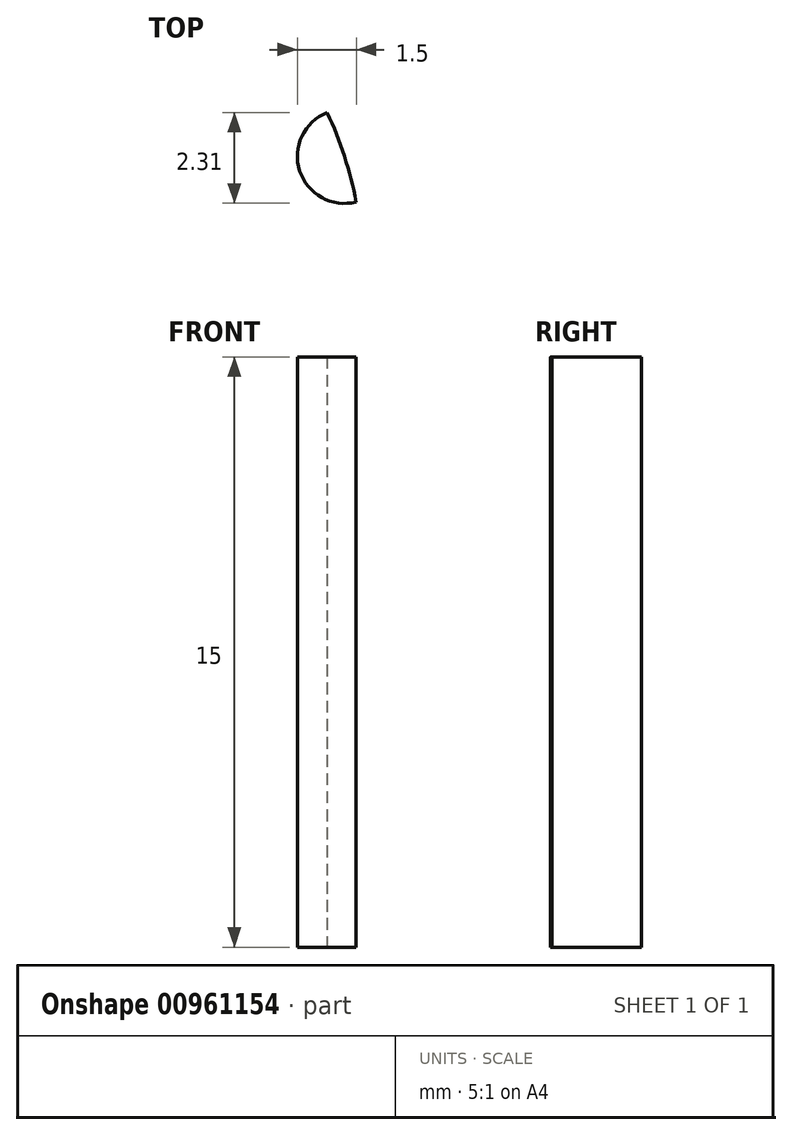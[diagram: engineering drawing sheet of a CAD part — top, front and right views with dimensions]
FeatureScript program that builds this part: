
annotation { "Feature Type Name" : "Feature", "Feature Type Description" : "" }
export const myFeature = defineFeature(function(context is Context, id is Id, definition is map)
    precondition{}
    {
        {
            var Q0;
            Q0=qCreatedBy(makeId("Top.planeOp"),FACE);
            var sketch = newSketch(context, id + "F0", { "sketchPlane" : qUnion([Q0])});
            skCircle(sketch, "E0", {"center": v(0, 0) * mm, "radius": 9.53 * mm});
            skCircle(sketch, "E1", {"center": v(0, 9.53) * mm, "radius": 1.2 * mm});
            skCircle(sketch, "E2.1.0", {"center": v(-5.6, 7.7) * mm, "radius": 1.2 * mm});
            skCircle(sketch, "E2.2.0", {"center": v(-9.06, 2.94) * mm, "radius": 1.2 * mm});
            skCircle(sketch, "E2.3.0", {"center": v(-9.06, -2.94) * mm, "radius": 1.2 * mm});
            skCircle(sketch, "E2.4.0", {"center": v(-5.6, -7.7) * mm, "radius": 1.2 * mm});
            skCircle(sketch, "E2.5.0", {"center": v(0, -9.53) * mm, "radius": 1.2 * mm});
            skCircle(sketch, "E2.6.0", {"center": v(5.6, -7.7) * mm, "radius": 1.2 * mm});
            skCircle(sketch, "E2.7.0", {"center": v(9.06, -2.94) * mm, "radius": 1.2 * mm});
            skCircle(sketch, "E2.8.0", {"center": v(9.06, 2.94) * mm, "radius": 1.2 * mm});
            skCircle(sketch, "E2.9.0", {"center": v(5.6, 7.7) * mm, "radius": 1.2 * mm});
            skSolve(sketch);
        }
        {
            var Q0;
            Q0=makeQuery(id+"F0.imprint","IMPRINT",FACE,{"disambiguationData":[TD([[makeQuery(id+"F0.imprint","IMPRINT",EDGE,{"derivedFrom":makeQuery(id+"FEj0pKjeV3EPrXN_0.opExtrude","CAP_EDGE",EDGE,{"disambiguationData":[OSD([sQuery(id+"FnyDLRzuZAjllcN_0.wireOp",EDGE,"B28xbMlO-8jRy-t1He-3Cjg-Zcp7sFitJE6t")])],"isStart":false})}),1.0]])]});
            var Q1;
            Q1=makeQuery(id+"F0.imprint","IMPRINT",FACE,{"disambiguationData":[TD([[makeQuery(id+"F0.imprint","IMPRINT",EDGE,{"derivedFrom":makeQuery(id+"FEj0pKjeV3EPrXN_0.opExtrude","CAP_EDGE",EDGE,{"disambiguationData":[OSD([sQuery(id+"FnyDLRzuZAjllcN_0.wireOp",EDGE,"B28xbMlO-8jRy-t1He-3Cjg-Zcp7sFitJE6t")])],"isStart":false})}),-1.0]])]});
            var Q2;
            Q2=makeQuery(id+"F0.imprint","IMPRINT",FACE,{"disambiguationData":[TD([[makeQuery(id+"F0.imprint","IMPRINT",EDGE,{"derivedFrom":makeQuery(id+"FEj0pKjeV3EPrXN_0.opExtrude","CAP_EDGE",EDGE,{"disambiguationData":[OSD([sQuery(id+"FnyDLRzuZAjllcN_0.wireOp",EDGE,"aedGRgQp-DsnF-1YjR-m7Mz-ZJWIFUI06pXP")])],"isStart":false})}),-1.0]])]});
            var Q3;
            {var subQ0=sQuery(id+"F0.wireOp",EDGE,"E2.8.0");var subQ1=sQuery(id+"F0.wireOp",EDGE,"E0");var subQ17=makeQuery(id+"F0.imprint","INTERSECT",VERTEX,{"disambiguationData":[OD(0.0)],"derivedFrom":[subQ1,subQ0]});Q3=makeQuery(id+"F0.imprint","IMPRINT",FACE,{"disambiguationData":[TD([[makeQuery(id+"F0.imprint","IMPRINT",EDGE,{"disambiguationData":[TD([[subQ17,-1.0]])],"derivedFrom":subQ1}),1.0]])]});}
            extrude(context, id + "F1", {"entities" : qUnion([Q0, Q1, Q2, Q3]), "depth" : 15 * mm, "offsetDistance" : 25 * mm});
        }
        {
            var Q0;
            Q0=makeQuery(id+"F1.opExtrude","CAP_FACE",FACE,{"disambiguationData":[OSD([sQuery(id+"F0.wireOp",EDGE,"E0")])],"isStart":false});
            var sketch = newSketch(context, id + "F2", { "sketchPlane" : qUnion([Q0])});
            skCircle(sketch, "E3", {"center": v(0, 0) * mm, "radius": 3 * mm});
            skSolve(sketch);
        }
        {
            var Q0;
            Q0=qSketchRegion(id+"F2",true);
            extrude(context, id + "F3", {"entities" : qUnion([Q0]), "operationType" : NewBodyOperationType.REMOVE, "endBound" : BoundingType.THROUGH_ALL, "oppositeDirection" : true, "depth" : 25 * mm, "offsetDistance" : 25 * mm});
        }
        {
            var Q0;
            Q0=makeQuery(id+"F1.opExtrude","CAP_FACE",FACE,{"disambiguationData":[OSD([sQuery(id+"F0.wireOp",EDGE,"E0"),sQuery(id+"F0.wireOp",EDGE,"E1"),sQuery(id+"F0.wireOp",EDGE,"E2.1.0"),sQuery(id+"F0.wireOp",EDGE,"E2.2.0"),sQuery(id+"F0.wireOp",EDGE,"E2.3.0"),sQuery(id+"F0.wireOp",EDGE,"E2.4.0"),sQuery(id+"F0.wireOp",EDGE,"E2.5.0"),sQuery(id+"F0.wireOp",EDGE,"E2.6.0"),sQuery(id+"F0.wireOp",EDGE,"E2.7.0"),sQuery(id+"F0.wireOp",EDGE,"E2.8.0"),sQuery(id+"F0.wireOp",EDGE,"E2.9.0")])],"isStart":false});
            var sketch = newSketch(context, id + "F4", { "sketchPlane" : qUnion([Q0])});
            skCircle(sketch, "E4.cCircle", {"center": v(0, 0) * mm, "radius": 5 * mm, "construction": true});
            skLineSegment(sketch, "E4.0", {"start": v(5.77, 0) * mm, "end": v(2.89, -5) * mm});
            skLineSegment(sketch, "E4.1", {"start": v(2.89, -5) * mm, "end": v(-2.89, -5) * mm});
            skLineSegment(sketch, "E4.2", {"start": v(-2.89, -5) * mm, "end": v(-5.77, 0) * mm});
            skLineSegment(sketch, "E4.3", {"start": v(-5.77, 0) * mm, "end": v(-2.89, 5) * mm});
            skLineSegment(sketch, "E4.4", {"start": v(-2.89, 5) * mm, "end": v(2.89, 5) * mm});
            skLineSegment(sketch, "E4.5", {"start": v(2.89, 5) * mm, "end": v(5.77, 0) * mm});
            skPoint(sketch, "E4.0.midPoint", {"position": v(4.33, -2.5) * mm});
            skSolve(sketch);
        }
        {
            var Q0;
            Q0=makeQuery(id+"F4.imprint","IMPRINT",FACE,{"disambiguationData":[TD([[makeQuery(id+"F4.imprint","IMPRINT",EDGE,{"derivedFrom":sQuery(id+"F4.wireOp",EDGE,"E4.0")}),-1.0]])]});
            extrude(context, id + "F5", {"entities" : qUnion([Q0]), "operationType" : NewBodyOperationType.REMOVE, "oppositeDirection" : true, "depth" : 10 * mm, "offsetDistance" : 25 * mm});
        }
    });
